# Revit family: FU_Inspec_Grade_4-2
name_source: partatom
category: Furniture
units: mm (PartAtom-declared; Revit-internal decimal feet)

## family parameters
Always vertical = Yes
Cut with Voids When Loaded = No
OmniClass Number = 23.40.20.00
OmniClass Title = General Furniture and Specialties
Room Calculation Point = No
Shared = No
Work Plane-Based = No

## types (3) — shared parameters
Assembly Code = E2020
Depth = 540 mm  [stored 1.77165 ft]
Height = 990 mm  [stored 3.24803 ft]
Keynote = 46.B
Manufacturer = Inspec
Seat Pad Material = Fabric - Divina Beige
URL = https://inspecfurniture.com
Weight = 6.5
Width = 480 mm  [stored 1.5748 ft]
zero-valued in all types: Default Elevation

## per-type parameters (varying)
| type | Description | Frame Material | Model | Seat Material |
| Grade 4.2 - Blue - Blue | Counter stool with recycled polypropylene seat and back on on powder coated or chromium plated steel tubular frame and footrest. Seat upholstered | Colour - Coated - Blue Green | Grade 4.2 | Colour - Coated - Blue Green |
| Grade 4.1 - Chrome - Blue | Counter stool with recycled polypropylene seat and back on on powder coated or chromium plated steel tubular frame and footrest | Metal - Chrome - Polished | Grade 4.1 | Colour - Coated - Blue Green |
| Grade 4.3 - Beige - Blue | Counter stool with fully upholstered recycled polypropylene seat and back on on powder coated or chromium plated steel tubular frame and footrest. | Colour - Coated - Blue Green | Grade 4.3 | Fabric - Divina Beige |

note: [stored X ft] marks values corroborated as IEEE doubles in the binary element streams (Revit-internal decimal feet)

## geometry (parser evidence)
native form markers: Blend x451, Sweep x2
no freeform markers — native parametric forms only
